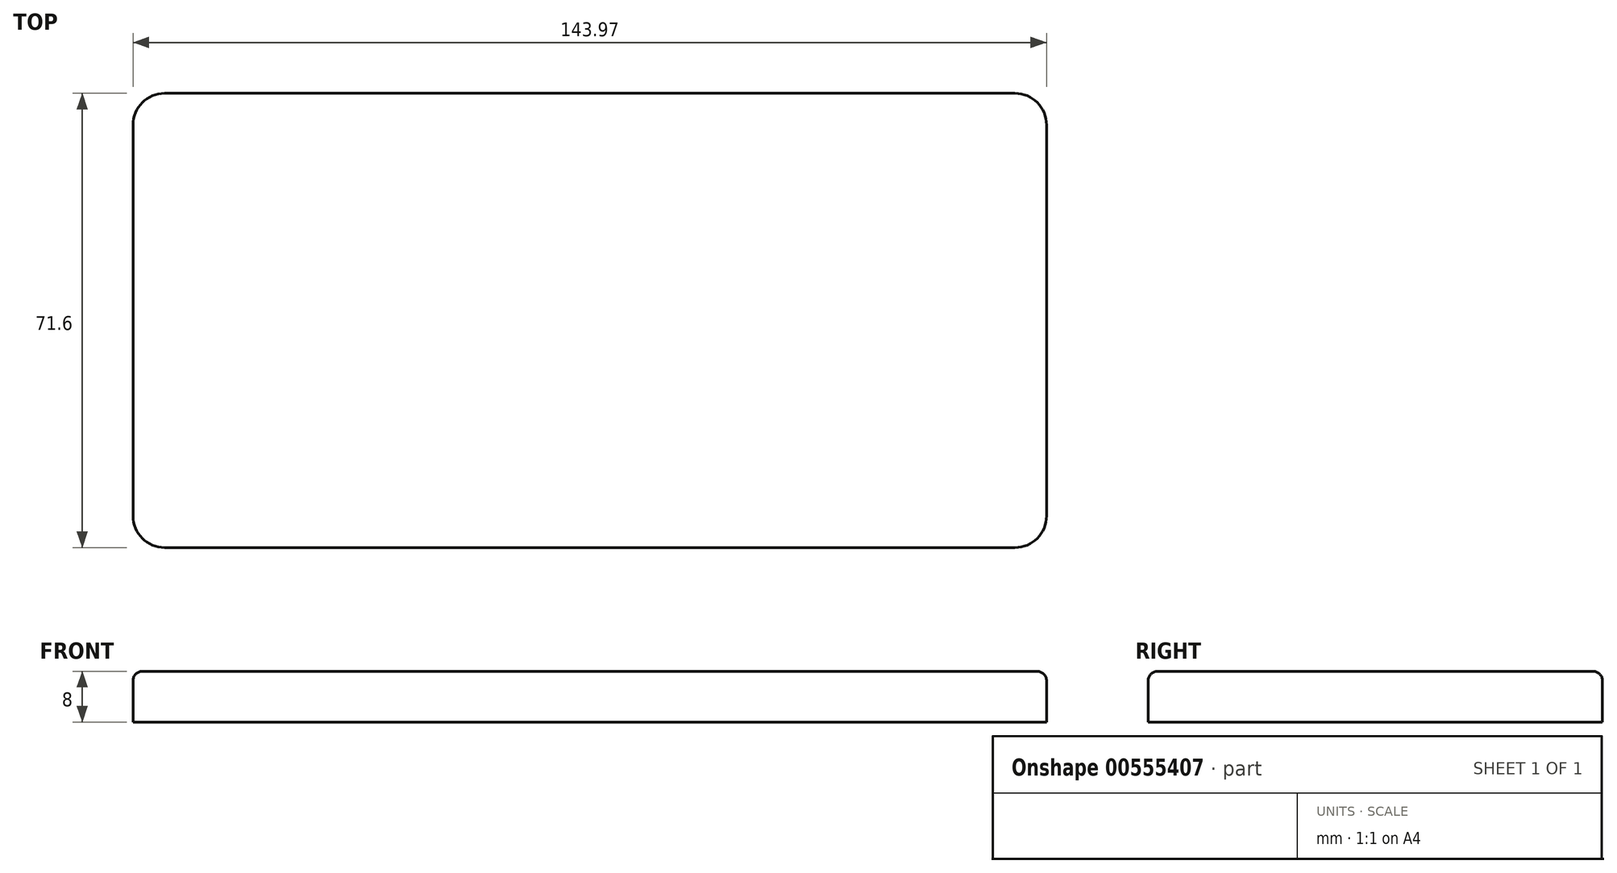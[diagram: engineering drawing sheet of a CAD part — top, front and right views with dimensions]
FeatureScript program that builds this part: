
annotation { "Feature Type Name" : "Feature", "Feature Type Description" : "" }
export const myFeature = defineFeature(function(context is Context, id is Id, definition is map)
    precondition{}
    {
        {
            var Q0;
            Q0=qCreatedBy(makeId("Top.planeOp"),FACE);
            var sketch = newSketch(context, id + "F0", { "sketchPlane" : qUnion([Q0])});
            skLineSegment(sketch, "E0.bottom", {"start": v(-67.53, 56.38) * mm, "end": v(66.44, 56.38) * mm});
            skLineSegment(sketch, "E0.top", {"start": v(-67.53, -15.22) * mm, "end": v(66.44, -15.22) * mm});
            skLineSegment(sketch, "E0.left", {"start": v(-72.53, 51.38) * mm, "end": v(-72.53, -10.22) * mm});
            skLineSegment(sketch, "E0.right", {"start": v(71.44, 51.38) * mm, "end": v(71.44, -10.22) * mm});
            skPoint(sketch, "E1.visualSharp", {"position": v(-72.53, -15.22) * mm});
            skArc(sketch, "E1.filletArc", {"start": v(-72.53, -10.22) * mm, "mid": v(-71.07, -13.76) * mm, "end": v(-67.53, -15.22) * mm});
            skPoint(sketch, "E2.visualSharp", {"position": v(-72.53, 56.38) * mm});
            skArc(sketch, "E2.filletArc", {"start": v(-67.53, 56.38) * mm, "mid": v(-71.07, 54.92) * mm, "end": v(-72.53, 51.38) * mm});
            skPoint(sketch, "E3.visualSharp", {"position": v(71.44, 56.38) * mm});
            skArc(sketch, "E3.filletArc", {"start": v(71.44, 51.38) * mm, "mid": v(69.97, 54.92) * mm, "end": v(66.44, 56.38) * mm});
            skPoint(sketch, "E4.visualSharp", {"position": v(71.44, -15.22) * mm});
            skArc(sketch, "E4.filletArc", {"start": v(66.44, -15.22) * mm, "mid": v(69.97, -13.76) * mm, "end": v(71.44, -10.22) * mm});
            skSolve(sketch);
        }
        {
            var Q0;
            Q0=makeQuery(id+"F0.imprint","IMPRINT",FACE,{"disambiguationData":[TD([[makeQuery(id+"F0.imprint","IMPRINT",EDGE,{"derivedFrom":sQuery(id+"F0.wireOp",EDGE,"E0.bottom")}),-1.0]])]});
            extrude(context, id + "F1", {"entities" : qUnion([Q0]), "depth" : 8 * mm, "offsetDistance" : 25 * mm});
        }
        {
            var Q0;
            Q0=makeQuery(id+"F1.opExtrude","CAP_FACE",FACE,{"disambiguationData":[OSD([sQuery(id+"F0.wireOp",EDGE,"E0.bottom"),sQuery(id+"F0.wireOp",EDGE,"E0.top"),sQuery(id+"F0.wireOp",EDGE,"E0.left"),sQuery(id+"F0.wireOp",EDGE,"E0.right"),sQuery(id+"F0.wireOp",EDGE,"E1.filletArc"),sQuery(id+"F0.wireOp",EDGE,"E2.filletArc"),sQuery(id+"F0.wireOp",EDGE,"E3.filletArc"),sQuery(id+"F0.wireOp",EDGE,"E4.filletArc")])],"isStart":false});
            fillet(context, id + "F2", {"entities" : qUnion([Q0]), "radius" : 1.5 * mm, "tangentPropagation" : true, "allowEdgeOverflow" : false});
        }
    });
